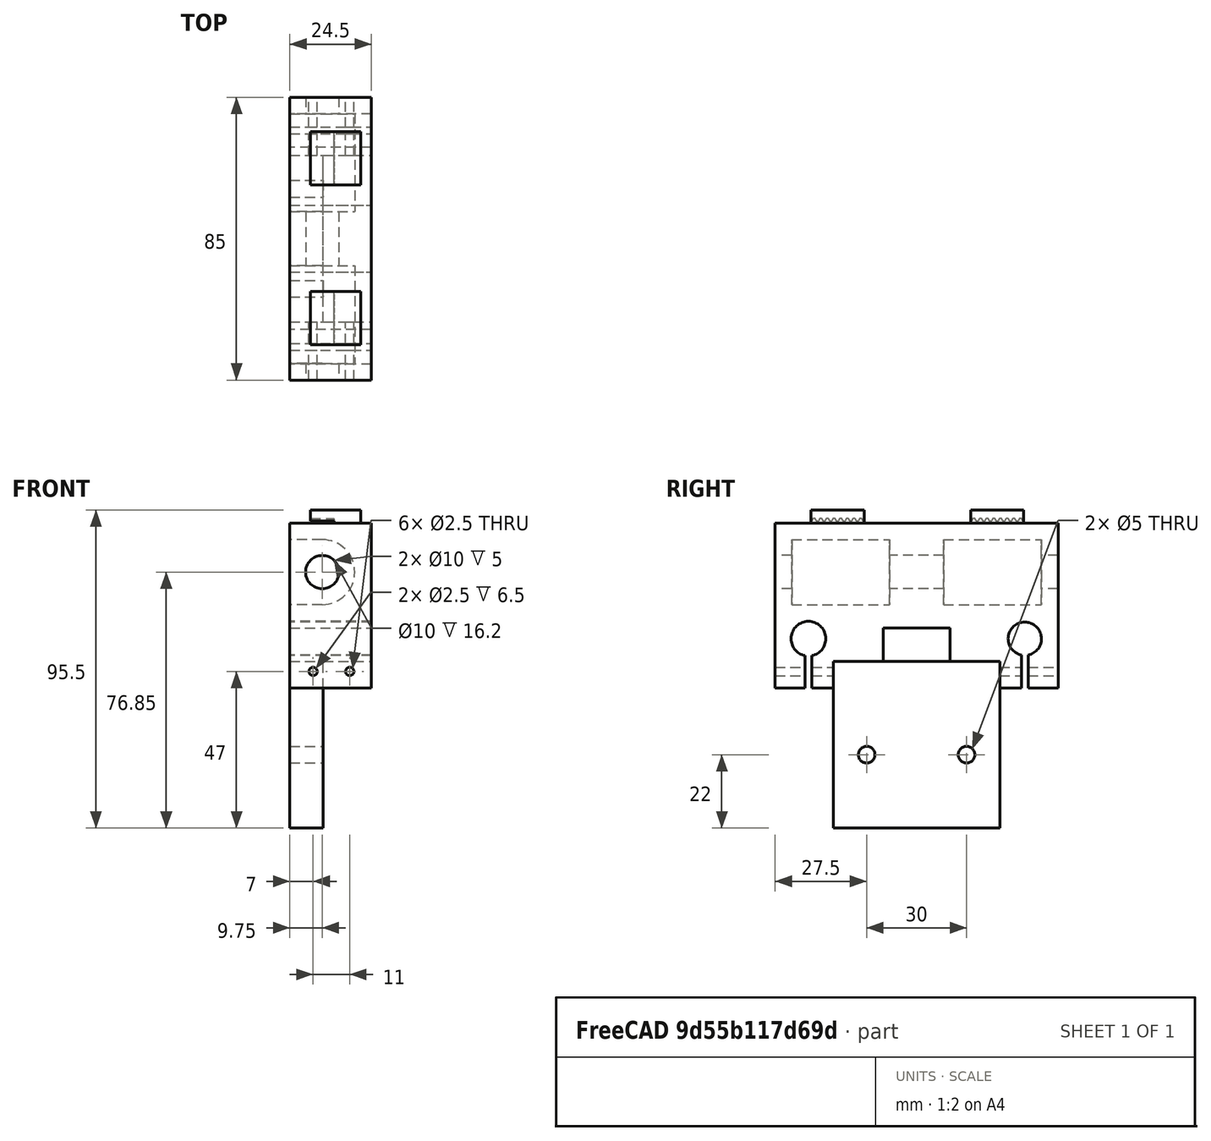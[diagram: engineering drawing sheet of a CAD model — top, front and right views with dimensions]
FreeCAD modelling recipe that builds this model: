
FCSTD DOCUMENT  (FreeCAD 0.18R16110 (Git))
Label: x-mount-right
License: All rights reserved
LicenseURL: http://en.wikipedia.org/wiki/All_rights_reserved
objects: Part::Cut×18, Part::Cylinder×10, Part::Box×9, Part::Extrusion×8, Part::MultiFuse×5, Spreadsheet::Sheet×2, Sketcher::SketchObject×1, Mesh::Feature×1
note: 51 computed .brp shape members not serialized (recipe doc carries the construction recipe); baked Part::Feature solids carry a one-line shape summary decoded from their .brp

FEATURE [Part::Box] Box023  label="Quader014"
  AttacherType = Attacher::AttachEngine3D
  Height = 19.5
  Length = 10
  Placement = pos=(0,0,-9.75) rot=(0,0,1;0rad)
  Width = 29.4
  expr: Width = Spreadsheet.x_hlinear
  expr: Placement.Base.z = -Spreadsheet.x_dlinear / 2
  expr: Height = Spreadsheet.x_dlinear
FEATURE [Part::Cylinder] Cylinder046  label="y_Führung003"
  Angle = 360
  AttacherType = Attacher::AttachEngine3D
  Height = 95
  Placement = pos=(-9.75,0,29.85) rot=(-1,0,0;1.5708rad)
  Radius = 5
  expr: Placement.Base.z = Spreadsheet.x_dlinear / 2 + Spreadsheet.tolerance / 2 + Spreadsheet.x_df + Spreadsheet.y_swand * 2
  expr: Height = Spreadsheet.E24 + 10
  expr: Placement.Base.x = -Spreadsheet.x_dlinear / 2
  expr: Radius = Spreadsheet.y_df / 2
FEATURE [Part::Cylinder] Cylinder045  label="Zylinder036"
  Angle = 360
  AttacherType = Attacher::AttachEngine3D
  Height = 24.5
  Placement = pos=(-24.5,78.85,9.85) rot=(0,1,0;1.5708rad)
  Radius = 5.2
  expr: Placement.Base.z = Spreadsheet.x_dlinear / 2 + Spreadsheet.tolerance / 2
  expr: Height = Spreadsheet.E23
  expr: Placement.Base.y = Spreadsheet.x_dlinear / 2 + Spreadsheet.x_swand + Spreadsheet.x_sfa + Spreadsheet.tolerance / 2
  expr: Placement.Base.x = -Spreadsheet.E23
  expr: Radius = Spreadsheet.x_df / 2 + Spreadsheet.tolerance
FEATURE [Part::Cylinder] Cylinder043  label="y_lineaer"
  Angle = 360
  AttacherType = Attacher::AttachEngine3D
  Height = 29.4
  Placement = pos=(0,0,0) rot=(-1,0,0;1.5708rad)
  Radius = 9.75
  expr: Height = Spreadsheet.x_hlinear
  expr: Radius = Spreadsheet.x_dlinear / 2
FEATURE [Part::MultiFuse] Fusion019  label="y_linear"
  Placement = pos=(-9.75,8.85,29.85) rot=(0,0,1;0rad)
  Shapes = -> [Cylinder043,Box023]
  expr: Placement.Base.y = Spreadsheet.E27 + Spreadsheet.y_swand
  expr: Placement.Base.x = -Spreadsheet.x_dlinear / 2
  expr: Placement.Base.z = Spreadsheet.x_dlinear / 2 + Spreadsheet.tolerance / 2 + Spreadsheet.x_df + Spreadsheet.y_swand * 2
FEATURE [Part::MultiFuse] Fusion020  label="y_linear001"
  Placement = pos=(-9.75,54.45,29.85) rot=(0,0,1;0rad)
  Shapes = -> [Cylinder043,Box023]
  expr: Placement.Base.y = Spreadsheet.x_swand + Spreadsheet.x_dlinear / 2 + Spreadsheet.tolerance / 2 - Spreadsheet.x_df / 2 - Spreadsheet.y_swand * 2 + Spreadsheet.E24 - Spreadsheet.x_hlinear
  expr: Placement.Base.x = -Spreadsheet.x_dlinear / 2
  expr: Placement.Base.z = Spreadsheet.x_dlinear / 2 + Spreadsheet.tolerance / 2 + Spreadsheet.x_df + Spreadsheet.y_swand * 2
FEATURE [Part::Cylinder] Cylinder044  label="Zylinder035"
  Angle = 360
  AttacherType = Attacher::AttachEngine3D
  Height = 24.5
  Placement = pos=(-24.5,13.85,9.85) rot=(0,1,0;1.5708rad)
  Radius = 5
  expr: Placement.Base.z = Spreadsheet.x_dlinear / 2 + Spreadsheet.tolerance / 2
  expr: Height = Spreadsheet.E23
  expr: Placement.Base.y = Spreadsheet.x_swand + Spreadsheet.x_dlinear / 2 + Spreadsheet.tolerance / 2
  expr: Placement.Base.x = -Spreadsheet.E23
  expr: Radius = Spreadsheet.x_df / 2
FEATURE [Part::Box] Box022  label="x_mount"
  AttacherType = Attacher::AttachEngine3D
  Height = 49.5
  Length = 24.5
  Placement = pos=(-24.5,3.85,-5) rot=(0,0,1;0rad)
  Width = 85
  expr: Placement.Base.z = Spreadsheet.E28
  expr: Height = Spreadsheet.E25
  expr: Placement.Base.y = Spreadsheet.E27
  expr: Placement.Base.x = Spreadsheet.E26
  expr: Width = Spreadsheet.E24
  expr: Length = Spreadsheet.E23
FEATURE [Part::Cut] Cut037
  Base = -> Box022
  Tool = -> Fusion019
FEATURE [Part::Cut] Cut038  label="x_mount_left"
  Base = -> Cut037
  Tool = -> Fusion020
FEATURE [Part::Cut] Cut039
  Base = -> Cut038
  Tool = -> Cylinder044
FEATURE [Part::Cut] Cut040  label="x_mount_left001"
  Base = -> Cut039
  Tool = -> Cylinder045
FEATURE [Part::Cylinder] Cylinder056  label="Zylinder046"
  Angle = 360
  AttacherType = Attacher::AttachEngine3D
  Height = 25
  Placement = pos=(-7,25,0) rot=(1,0,0;1.5708rad)
  Radius = 1.25
FEATURE [Part::Box] Box030  label="Quader021"
  AttacherType = Attacher::AttachEngine3D
  Height = 18
  Length = 27.5
  Placement = pos=(-26,77.85,-9) rot=(0,0,1;0rad)
  Width = 2
  expr: Placement.Base.y = Spreadsheet.x_swand + Spreadsheet.x_dlinear / 2 + Spreadsheet.tolerance / 2 - 1 + Spreadsheet.x_sfa
  expr: Length = Spreadsheet.E23 + 3
FEATURE [Part::Cylinder] Cylinder059  label="Zylinder049"
  Angle = 360
  AttacherType = Attacher::AttachEngine3D
  Height = 25
  Placement = pos=(-7,92,0) rot=(1,0,0;1.5708rad)
  Radius = 1.25
FEATURE [Part::Cylinder] Cylinder057  label="Zylinder047"
  Angle = 360
  AttacherType = Attacher::AttachEngine3D
  Height = 25
  Placement = pos=(-18,92,0) rot=(1,0,0;1.5708rad)
  Radius = 1.25
FEATURE [Part::Box] Box033  label="Quader024"
  AttacherType = Attacher::AttachEngine3D
  Height = 18
  Length = 24.5
  Placement = pos=(0,-56.35,-5) rot=(0,0,1;0rad)
  Width = 20
  expr: Placement.Base.y = -Spreadsheet.E27 - Spreadsheet.E24 / 2 - 10
  expr: Placement.Base.z = Spreadsheet.E28
  expr: Length = Spreadsheet.E23
FEATURE [Part::Cylinder] Cylinder058  label="Zylinder048"
  Angle = 360
  AttacherType = Attacher::AttachEngine3D
  Height = 25
  Placement = pos=(-18,25,0) rot=(1,0,0;1.5708rad)
  Radius = 1.25
FEATURE [Part::Box] Box029  label="Quader020"
  AttacherType = Attacher::AttachEngine3D
  Height = 18
  Length = 27.5
  Placement = pos=(-26,12.85,-9) rot=(0,0,1;0rad)
  Width = 2
  expr: Placement.Base.y = Spreadsheet.x_swand + Spreadsheet.x_dlinear / 2 + Spreadsheet.tolerance / 2 - 1
  expr: Length = Spreadsheet.E23 + 3
FEATURE [Part::Cut] Cut050  label="x_mount_left005"
  Base = -> Cut040
  Tool = -> Cylinder046
FEATURE [Part::Cut] Cut051
  Base = -> Cut050
  Tool = -> Cylinder056
FEATURE [Part::Cut] Cut052
  Base = -> Cut051
  Tool = -> Cylinder057
FEATURE [Part::Cut] Cut053
  Base = -> Cut052
  Tool = -> Cylinder058
FEATURE [Part::Cut] Cut054  label="x_mount_right"
  Base = -> Cut053
  Tool = -> Cylinder059
FEATURE [Part::Cut] Cut055
  Base = -> Cut054
  Tool = -> Box029
FEATURE [Part::Cut] Cut056  label="x_mount_right001"
  Base = -> Cut055
  Placement = pos=(0,0,0) rot=(0,0,1;3.14159rad)
  Tool = -> Box030
FEATURE [Part::Cut] Cut058  label="x_mount_right002"
  Base = -> Cut056
  Tool = -> Box033
FEATURE [Part::Box] Box048  label="Quader027"
  AttacherType = Attacher::AttachEngine3D
  Height = 15
  Length = 16
  Width = 4
FEATURE [Part::Box] Box049  label="Quader028"
  AttacherType = Attacher::AttachEngine3D
  Height = 12
  Length = 16
  Placement = pos=(0,-4.3,-5) rot=(0,0,1;0rad)
  Width = 5
FEATURE [Part::Box] Box057  label="Quader036"
  AttacherType = Attacher::AttachEngine3D
  Height = 8
  Length = 24.5
  Placement = pos=(0,-71.35,-5) rot=(0,0,1;0rad)
  Width = 50
  expr: Length = Spreadsheet.E23
  expr: Placement.Base.y = -Spreadsheet.E27 - Spreadsheet.E24 / 2 - 25
FEATURE [Part::Box] Box058  label="Quader037"
  AttacherType = Attacher::AttachEngine3D
  Height = 50
  Length = 10
  Placement = pos=(0,-71.35,-47) rot=(0,0,1;0rad)
  Width = 50
  expr: Placement.Base.y = -Spreadsheet.E27 - Spreadsheet.E24 / 2 - 25
FEATURE [Part::Cut] Cut097  label="x_mount_right003"
  Base = -> Cut058
  Tool = -> Box057
FEATURE [Part::MultiFuse] Fusion047  label="x_mount_right004"
  Shapes = -> [Cut097,Box058]
FEATURE [Part::Cylinder] Cylinder083  label="Zylinder071"
  Angle = 360
  AttacherType = Attacher::AttachEngine3D
  Height = 10
  Placement = pos=(0,-61.35,-25) rot=(0,1,0;1.5708rad)
  Radius = 2.5
  expr: Radius = 2.5
  expr: Placement.Base.y = -Spreadsheet.E27 - Spreadsheet.E24 / 2 - 15
FEATURE [Part::Cut] Cut098
  Base = -> Fusion047
  Tool = -> Cylinder083
FEATURE [Part::Cylinder] Cylinder084  label="Zylinder072"
  Angle = 360
  AttacherType = Attacher::AttachEngine3D
  Height = 10
  Placement = pos=(0,-31.35,-25) rot=(0,1,0;1.5708rad)
  Radius = 2.5
  expr: Radius = 2.5
  expr: Placement.Base.y = -Spreadsheet.E27 - Spreadsheet.E24 / 2 + 15
FEATURE [Part::Cut] Cut099  label="x_mount_right005"
  Base = -> Cut098
  Tool = -> Cylinder084
FEATURE [Spreadsheet::Sheet] Spreadsheet
  cells = A1=Toleranz; B1(tolerance)=0.2; D1=x_pos; E1=0; G1=y_pos; H1=0; A2=z_pos; B2=-10; E2=min 0 / max 297; G2=min y_pos; H2=94; I2=max 560; A3=Z-Support; D3=X-Support; G3=y-Support; J3=structure; A4=Führung d; B4(z_df)=8; D4=Führung d; E4(x_df)=10; G4=Führung d; H4(y_df)=10; J4=profil B; K4=20; A5=Führung l; B5(z_fl)==Spreadsheet.z_hub + Spreadsheet.z_hmount * 2 + Spreadsheet.z_hs - 5; D5=Führung l; E5(x_lf)=420; F5=400; G5=Führung l; H5(y_fl)=700; I5=500; J5=distanz Führung; K5=3; A6=Abstand Führung z_sfa; B6(z_sfa)==(z_dlinear + 2 * z_swand + 2 * z_sriemenspiel + z_lriemen) * 1 + (2 * x_hlinear + +z_swand - z_df + 4 * tolerance) * 0; D6=Abstand Führung x_sfa; E6(x_sfa)=65; G6=Abstand Fü y_sfa; H6(y_sfa)==x_lf - x_dlinear - 2 * y_swand; J6=höhe; K6=300; J7=add to Top; K7=18; A8=Schlittenwand swand; B8(z_swand)=5; D8=Schlitten swand; E8(x_swand)=4; G8=y_swand; H8(y_swand)=5; A9=Schlittenlänge z_ls; B9(z_ls)==z_sfa + z_dlinear; D9=Schlittenlänge; E9(x_ls)==z_lmount; A10=Schlittenbreite z_bs; B10(z_bs)==2 * z_swand + z_dlinear; D10=Schlitten breite; E10(x_bs)==Spreadsheet.x_swand * 2 + Spreadsheet.x_dlinear + Spreadsheet.x_sfa; G10=d Antrieb; H10=5; A11=Schlittenhöhe z_hs; B11(z_hs)==z_hlinear + 2 * z_swand; D11=schlittenhöhe x_hs; E11(x_hs)==x_dlinear + x_swand; A12=Hub; B12(z_hub)=100; A14=Linearlager; A15=durchmesser z_dlinear; B15(z_dlinear)=15.4; D15=durchmesser x_dlinear; E15(x_dlinear)=19.5; A16=höhe z_hlinear; B16(z_hlinear)=24.4; D16=höhe x_hlinear; E16(x_hlinear)=29.4; A18=Riemenscheibe bohrung; B18=5; A19=durchmesser z_driemen; B19(z_driemen)=16; D19=dopper pulley; E19=27.5; F19=15.8; A20=länge z_lriemen; B20(z_lriemen)=28; D20=pulley; E20=15.25; F20=15.8; G20=20 Zähne: 2* 180 °; H20=2mm*20 Zähne; I20==40mm; A21=spiel riemenscheibe z_sriemenspiel; B21(z_sriemenspiel)=2; A22=Bohreung z_dbohrung; B22(z_dbohrung)=8; C22=durchmesser Laufbuchse; D22=x_mount; A23=Bohrunlänge z_lbohrung; B23(z_lbohrung)=5; D23=Breite x_mount; E23==y_swand + x_dlinear; A24=riemenbreite z_briemen; B24(z_briemen)=6; D24=Länge x_mount; E24==x_sfa + x_df + y_swand * 2; A25=pitch z_rriemenpitch; B25(z_rriemepitch)=7; D25=Höhe x_mount; E25==y_swand * 2 + x_df + +y_swand + x_dlinear + y_swand; A26=achsen pos y; B26==-Spreadsheet.z_driemen / 2 - Spreadsheet.tolerance * 2; D26= xpos; E26==-Spreadsheet.E23; A27=achsen pos z; B27==(Spreadsheet.z_hub + Spreadsheet.z_hs + Spreadsheet.x_hs) / 2 + z_hmount - z_dbohrung / 2 - Spreadsheet.z_dbohrung / 2; D27=ypos; E27==Spreadsheet.x_swand + Spreadsheet.x_dlinear / 2 + Spreadsheet.tolerance / 2 - Spreadsheet.x_df / 2 - Spreadsheet.y_swand; D28= zpos; E28==-y_swand; A29=Mount; A30=Höhe mount; B30(z_hmount)=20; A31=Länge mount; B31(z_lmount)==z_swand * 2 + z_df + z_sfa; A32=Breite mount; B32(z_bmount)==(Spreadsheet.z_swand + Spreadsheet.z_driemen + Spreadsheet.tolerance * 2) * 0 + 26; A34=Nema; D34=Nema x; A35=Länge; B35(lnema)=42; D35(nema_x_b)=42; A36=Breite; B36(bnema)=42; D36=42; A37=Höhe; B37(hnema)=34; D37(nema_x_h)=48; A38=Achslänge; B38(lanema)=20; D38(nema_x_al)=22; A39=achsen pos y; B39(nema_achse_y)==sqrt(B43 ^ 2 - (B27 - B40) ^ 2) + B26; E39(nemax_achsey)==Spreadsheet.x_swand + Spreadsheet.x_df / 2 + Spreadsheet.x_dlinear / 2 + Spreadsheet.nema_x_h + 2; A40=achsen pos z; B40(nema_achse_z)==x_hs + lnema / 2 + 4; E40(nema_x_achsez)==-Spreadsheet.x_hs / 2; A41=achsen pos x; B41(nema_achse_x)==(z_lmount - z_lriemen) / 2 - z_sriemenspiel; E41(nema_x_achsex)==Spreadsheet.x_lf - Spreadsheet.nema_x_b / 2 - Spreadsheet.y_df; A42=länge zahnriemen; B42=200; C42=gerechnet; A43=abstand achsen; B43==(B42 - 40) / 2; C43==sqrt((Spreadsheet.B27 - Spreadsheet.nema_achse_z) ^ 2 + (-Spreadsheet.B26 + Spreadsheet.nema_achse_y) ^ 2) * 2 + 2 * pi * 7; D43=Zahnriemen x; D44=Breite; E44=6; A45=doppel pulley; D45=Höhe; E45==(Spreadsheet.F20 + Spreadsheet.tolerance * 2) * 0 + 15; A46= achse1  x pos; B46==z_lmount / 2 - (6.5 + 8.9) / 2; D46=Länge; E46==y_sfa + x_dlinear + y_swand * 2 + 2 + nema_x_b / 2; A47= achse2 xpos; B47==z_lmount / 2 + (6.5 + 8.9) / 2; B48==-atan((Spreadsheet.B27 - Spreadsheet.nema_achse_z) / (-Spreadsheet.B26 + Spreadsheet.nema_achse_y))
FEATURE [Spreadsheet::Sheet] Spreadsheet001
  cells = A1=abstand zähne; B1=2; A2=dicke; B2=1.38; A3=zahntiefe; B3=0.75; A4=r1; B4=0.555; A5=r2; B5=1; A6=r3; B6=0.15; A7=pitch; B7=0.254; A8=tolerance; B8=0.1
FEATURE [Sketcher::SketchObject] Sketch
  MapMode = 2
  Placement = pos=(0,0,0) rot=(0,1,0;3.14159rad)
  expr: Constraints[11] = Spreadsheet001.B5
  expr: Constraints[30] = Spreadsheet001.B1 / 2
  expr: Constraints[25] = Spreadsheet001.B2 - Spreadsheet001.B3
  expr: Constraints[16] = Spreadsheet001.B2 - Spreadsheet001.B3
  expr: Constraints[18] = Spreadsheet001.B6
  expr: Constraints[36] = Spreadsheet001.B6
  expr: Constraints[33] = Spreadsheet001.B2 - Spreadsheet001.B3
  expr: Constraints[17] = Spreadsheet001.B1 / 2
  expr: Constraints[9] = Spreadsheet001.B2 - Spreadsheet001.B3
  expr: Constraints[2] = Spreadsheet001.B2 - Spreadsheet001.B4
  sketch-geometry (16):
    g0: LineSegment [constr] StartX=0 StartY=0 StartZ=0 EndX=0 EndY=-0.825 EndZ=0
    g1: ArcOfCircle CenterX=0 CenterY=-0.825 CenterZ=0 NormalX=0 NormalY=0 NormalZ=1 AngleXU=0 Radius=0.555 StartAngle=3.59519 EndAngle=5.82959
    g2: LineSegment [constr] StartX=0 StartY=0 StartZ=0 EndX=0.4 EndY=0 EndZ=0
    g3: LineSegment [constr] StartX=0.4 StartY=0 StartZ=0 EndX=0.4 EndY=-0.63 EndZ=0
    g4: ArcOfCircle CenterX=0.4 CenterY=-0.63 CenterZ=0 NormalX=0 NormalY=0 NormalZ=1 AngleXU=0 Radius=1 StartAngle=3.2724 EndAngle=3.59519
    g5: LineSegment StartX=0 StartY=0 StartZ=0 EndX=-1 EndY=0 EndZ=0
    g6: LineSegment StartX=-1 StartY=0 StartZ=0 EndX=-1 EndY=-0.63 EndZ=0
    g7: ArcOfCircle CenterX=-0.740175 CenterY=-0.78 CenterZ=0 NormalX=0 NormalY=0 NormalZ=1 AngleXU=0 Radius=0.15 StartAngle=0.130807 EndAngle=1.5708
    g8: LineSegment StartX=-1 StartY=-0.63 StartZ=0 EndX=-0.740175 EndY=-0.63 EndZ=0
    g9: LineSegment [constr] StartX=0 StartY=0 StartZ=0 EndX=-0.4 EndY=0 EndZ=0
    g10: LineSegment [constr] StartX=-0.4 StartY=0 StartZ=0 EndX=-0.4 EndY=-0.63 EndZ=0
    g11: ArcOfCircle CenterX=-0.4 CenterY=-0.63 CenterZ=0 NormalX=0 NormalY=0 NormalZ=1 AngleXU=0 Radius=1 StartAngle=5.82959 EndAngle=6.15238
    g12: LineSegment StartX=0 StartY=0 StartZ=0 EndX=1 EndY=0 EndZ=0
    g13: LineSegment StartX=1 StartY=0 StartZ=0 EndX=1 EndY=-0.63 EndZ=0
    g14: LineSegment StartX=1 StartY=-0.63 StartZ=0 EndX=0.740175 EndY=-0.63 EndZ=0
    g15: ArcOfCircle CenterX=0.740175 CenterY=-0.78 CenterZ=0 NormalX=0 NormalY=0 NormalZ=1 AngleXU=0 Radius=0.15 StartAngle=1.5708 EndAngle=3.01079
  constraints (43):
    c: Coincident(g0,g-1)
    c: Vertical(g0)
    c: DistanceY(g0,g0) = 0.825
    c: Coincident(g1,g0)
    c: Coincident(g2,g-1)
    c: Horizontal(g2)
    c: DistanceX(g2,g2) = 0.4
    c: Coincident(g3,g2)
    c: Vertical(g3)
    c: DistanceY(g3,g3) = 0.63
    c: Coincident(g4,g3)
    c: Radius(g4) = 1
    c: Coincident(g5,g-1)
    c: Horizontal(g5)
    c: Coincident(g6,g5)
    c: Vertical(g6)
    c: DistanceY(g6,g6) = 0.63
    c: DistanceX(g5,g5) = 1
    c: Radius(g7) = 0.15
    c: Coincident(g8,g6)
    c: Horizontal(g8)
    c: Coincident(g9,g-1)
    c: Distance(g9) = 0.4
    c: Coincident(g10,g9)
    c: Vertical(g10)
    c: DistanceY(g10,g10) = 0.63
    c: Horizontal(g9)
    c: Coincident(g11,g10)
    c: Coincident(g12,g-1)
    c: Horizontal(g12)
    c: DistanceX(g12,g12) = 1
    c: Coincident(g13,g12)
    c: Vertical(g13)
    c: DistanceY(g13,g13) = 0.63
    c: Coincident(g14,g13)
    c: Horizontal(g14)
    c: Radius(g15) = 0.15
    c: Tangent(g15,g14) = -1.5708
    c: Tangent(g7,g8) = 1.5708
    c: Tangent(g7,g4) = 1.5708
    c: Tangent(g15,g11) = 1.5708
    c: Tangent(g4,g1) = -1.5708
    c: Tangent(g11,g1) = -1.5708
FEATURE [Part::Extrusion] Extrude001
  Base = -> Sketch
  Dir = (0,0,-1)
  DirMode = 2
  FaceMakerClass = Part::FaceMakerBullseye
  LengthFwd = 7
  LengthRev = 0
  Placement = pos=(2,0,0) rot=(0,0,1;0rad)
  Solid = true
  Symmetric = false
FEATURE [Part::Extrusion] Extrude003
  Base = -> Sketch
  Dir = (0,0,-1)
  DirMode = 2
  FaceMakerClass = Part::FaceMakerBullseye
  LengthFwd = 7
  LengthRev = 0
  Placement = pos=(6,0,0) rot=(0,0,1;0rad)
  Solid = true
  Symmetric = false
FEATURE [Part::Extrusion] Extrude004
  Base = -> Sketch
  Dir = (0,0,-1)
  DirMode = 2
  FaceMakerClass = Part::FaceMakerBullseye
  LengthFwd = 7
  LengthRev = 0
  Placement = pos=(10,0,0) rot=(0,0,1;0rad)
  Solid = true
  Symmetric = false
FEATURE [Part::Extrusion] Extrude
  Base = -> Sketch
  Dir = (0,0,-1)
  DirMode = 2
  FaceMakerClass = Part::FaceMakerBullseye
  LengthFwd = 7
  LengthRev = 0
  Solid = true
  Symmetric = false
FEATURE [Part::Extrusion] Extrude007
  Base = -> Sketch
  Dir = (0,0,-1)
  DirMode = 2
  FaceMakerClass = Part::FaceMakerBullseye
  LengthFwd = 7
  LengthRev = 0
  Placement = pos=(12,0,0) rot=(0,0,1;0rad)
  Solid = true
  Symmetric = false
FEATURE [Part::Extrusion] Extrude002
  Base = -> Sketch
  Dir = (0,0,-1)
  DirMode = 2
  FaceMakerClass = Part::FaceMakerBullseye
  LengthFwd = 7
  LengthRev = 0
  Placement = pos=(4,0,0) rot=(0,0,1;0rad)
  Solid = true
  Symmetric = false
FEATURE [Part::Extrusion] Extrude005
  Base = -> Sketch
  Dir = (0,0,-1)
  DirMode = 2
  FaceMakerClass = Part::FaceMakerBullseye
  LengthFwd = 7
  LengthRev = 0
  Placement = pos=(8,0,0) rot=(0,0,1;0rad)
  Solid = true
  Symmetric = false
FEATURE [Part::Extrusion] Extrude006
  Base = -> Sketch
  Dir = (0,0,-1)
  DirMode = 2
  FaceMakerClass = Part::FaceMakerBullseye
  LengthFwd = 7
  LengthRev = 0
  Placement = pos=(14,0,0) rot=(0,0,1;0rad)
  Solid = true
  Symmetric = false
FEATURE [Part::MultiFuse] Fusion030  label="Form Zahnriemen"
  Placement = pos=(15,0.1,7) rot=(0,0,1;3.14159rad)
  Shapes = -> [Extrude005,Extrude002,Extrude003,Extrude,Extrude001,Extrude004,Extrude007,Extrude006]
FEATURE [Part::Cut] Cut059
  Base = -> Box048
  Tool = -> Fusion030
FEATURE [Part::Cut] Cut062  label="Zahnriemen Befestigung002"
  Base = -> Cut059
  Placement = pos=(6.25,-78.15,44.5) rot=(0.57735,0.57735,0.57735;2.0944rad)
  Tool = -> Box049
  expr: Placement.Base.y = Spreadsheet.E27 - Spreadsheet.E24 + 3
  expr: Placement.Base.x = -3.5 + Spreadsheet.x_dlinear / 2
  expr: Placement.Base.z = Spreadsheet.E28 + Spreadsheet.E25
FEATURE [Part::Cut] Cut063  label="Zahnriemen Befestigung003"
  Base = -> Cut059
  Placement = pos=(6.25,-30.15,44.5) rot=(0.57735,0.57735,0.57735;2.0944rad)
  Tool = -> Box049
  expr: Placement.Base.y = Spreadsheet.E27 - 17 - 17
  expr: Placement.Base.x = Spreadsheet.x_dlinear / 2 - 3.5
  expr: Placement.Base.z = Spreadsheet.E28 + Spreadsheet.E25
FEATURE [Part::MultiFuse] Fusion048  label="x-mount-right"
  Placement = pos=(371,92.7,0) rot=(0,0,1;0rad)
  Shapes = -> [Cut099,Cut062,Cut063]
  expr: Placement.Base.y = (Spreadsheet.x_swand + Spreadsheet.x_dlinear / 2 + Spreadsheet.tolerance / 2 - Spreadsheet.x_df / 2 - Spreadsheet.y_swand) * 2 + Spreadsheet.E24 + Spreadsheet.H1
  expr: Placement.Base.x = -Spreadsheet.x_dlinear + Spreadsheet.y_sfa
FEATURE [Mesh::Feature] Mesh  label="x-mount-right(Meshed)"
